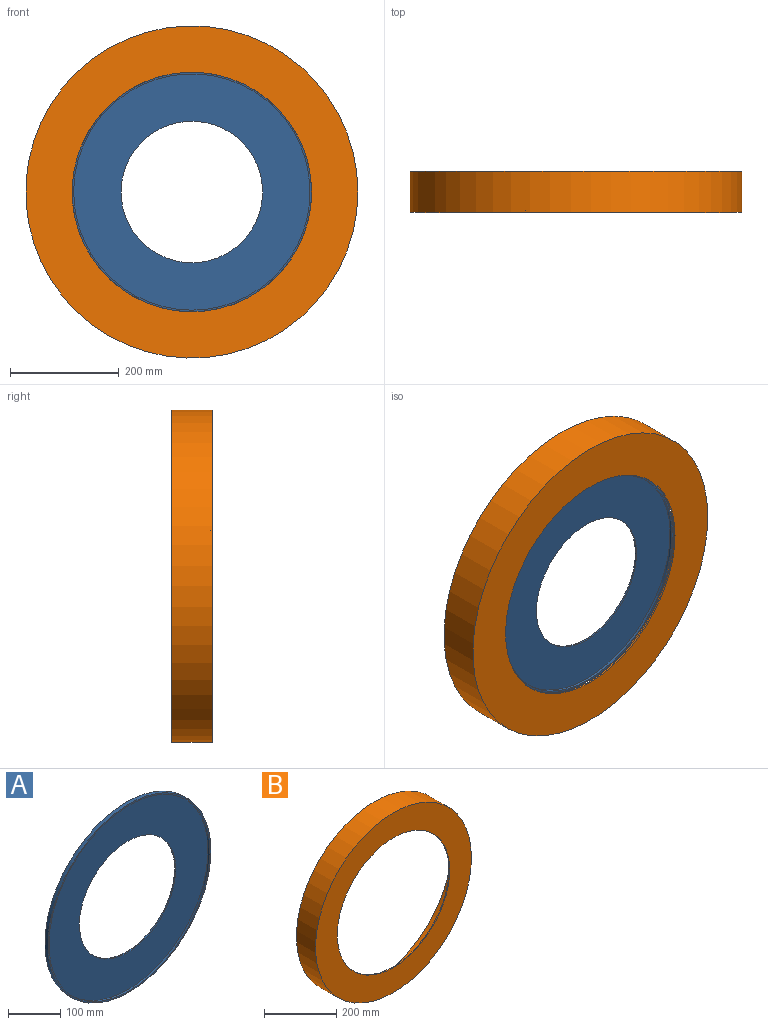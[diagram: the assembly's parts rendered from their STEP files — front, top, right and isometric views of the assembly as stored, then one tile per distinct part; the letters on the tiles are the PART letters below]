
ASSEMBLY  parts=2 mates=1
PART A: 6 faces, bbox 440x8x440 mm
  f0: cylinder r=220mm len=440mm, axis (0,1,0), area 11058.4mm2, adj f1,f2
  f1: plane 440x440mm, normal (0,-1,0), area 4118.6mm2, adj f0,f3
  f2: plane 440x440mm, normal (0,1,0), area 98960.2mm2, adj f0,f5
  f3: cylinder r=217mm len=434mm, axis (0,1,0), area 6817.3mm2, adj f1,f4
  f4: plane 434x434mm, normal (0,-1,0), area 94841.5mm2, adj f3,f5
  f5: cylinder r=130mm len=260mm, axis (0,-1,0), area 2450.4mm2, adj f2,f4
PART B: 6 faces, bbox 610x75x610 mm
  f0: cylinder r=305mm len=610mm, axis (0,1,0), area 143727.9mm2, adj f1,f2
  f1: plane 610x610mm, normal (0,-1,0), area 140193.6mm2, adj f0,f5
  f2: plane 610x610mm, normal (0,1,0), area 5720.8mm2, adj f0,f3
  f3: cylinder r=302mm len=604mm, axis (0,1,0), area 136621.6mm2, adj f2,f4
  f4: plane 604x604mm, normal (0,1,0), area 134472.7mm2, adj f3,f5
  f5: cylinder r=220mm len=440mm, axis (0,-1,0), area 4146.9mm2, adj f1,f4
PLACE A t=(0,-62,26)mm
PLACE B t=(0,0,26)mm
MATE cylindrical A.f0 <-> B.f0  axis (0,-1,0) through (0,-70,26)mm
